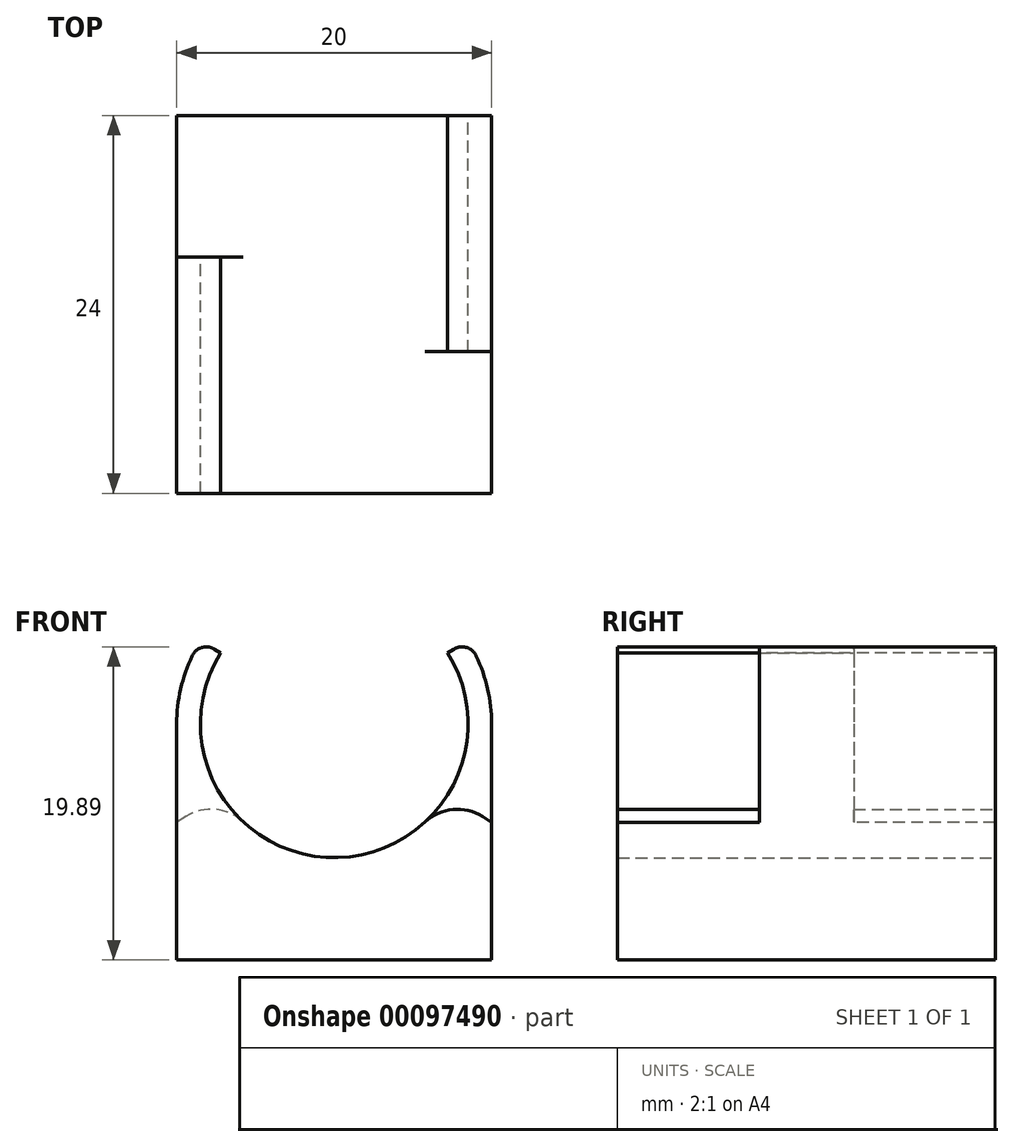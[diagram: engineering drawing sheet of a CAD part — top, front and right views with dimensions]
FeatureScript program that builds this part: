
annotation { "Feature Type Name" : "Feature", "Feature Type Description" : "" }
export const myFeature = defineFeature(function(context is Context, id is Id, definition is map)
    precondition{}
    {
        {
            var Q0;
            Q0=qCreatedBy(makeId("Front.planeOp"),FACE);
            var sketch = newSketch(context, id + "F0", { "sketchPlane" : qUnion([Q0])});
            skCircle(sketch, "E0", {"center": v(0, 0) * mm, "radius": 8.5 * mm});
            skCircle(sketch, "E1", {"center": v(0, 0) * mm, "radius": 10 * mm});
            skLineSegment(sketch, "E2", {"start": v(0, 10) * mm, "end": v(0, -10) * mm, "construction": true});
            skLineSegment(sketch, "E3", {"start": v(-8.48, 5.3) * mm, "end": v(0, 0) * mm});
            skLineSegment(sketch, "E4.MirrorCS", {"start": v(8.48, 5.3) * mm, "end": v(0, 0) * mm});
            skLineSegment(sketch, "E5.top", {"start": v(-10, -10) * mm, "end": v(10, -10) * mm});
            skLineSegment(sketch, "E5.left", {"start": v(-10, 0) * mm, "end": v(-10, -10) * mm});
            skLineSegment(sketch, "E5.right", {"start": v(10, 0) * mm, "end": v(10, -10) * mm});
            skLineSegment(sketch, "E6", {"start": v(0, -10) * mm, "end": v(0, -8.5) * mm});
            skLineSegment(sketch, "E7", {"start": v(0, 0) * mm, "end": v(10, -6.25) * mm});
            skLineSegment(sketch, "E8.MirrorCS", {"start": v(0, 0) * mm, "end": v(-10, -6.25) * mm});
            skSolve(sketch);
        }
        {
            var Q0;
            {var subQ0=sQuery(id+"F0.wireOp",EDGE,"E5.top");var subQ5=sQuery(id+"F0.wireOp",EDGE,"E5.right");var subQ7=makeQuery(id+"F0.imprint","INTERSECT",VERTEX,{"derivedFrom":[subQ0,subQ5]});Q0=makeQuery(id+"F0.imprint","IMPRINT",FACE,{"disambiguationData":[TD([[makeQuery(id+"F0.imprint","IMPRINT",EDGE,{"disambiguationData":[TD([[subQ7,1.0]])],"derivedFrom":subQ5}),-1.0]])]});}
            var Q1;
            {var subQ0=sQuery(id+"F0.wireOp",EDGE,"E5.top");var subQ5=sQuery(id+"F0.wireOp",EDGE,"E5.left");var subQ6=makeQuery(id+"F0.imprint","INTERSECT",VERTEX,{"derivedFrom":[subQ0,subQ5]});Q1=makeQuery(id+"F0.imprint","IMPRINT",FACE,{"disambiguationData":[TD([[makeQuery(id+"F0.imprint","IMPRINT",EDGE,{"disambiguationData":[TD([[subQ6,1.0]])],"derivedFrom":subQ5}),1.0]])]});}
            var Q2;
            {var subQ0=sQuery(id+"F0.wireOp",EDGE,"E6");Q2=makeQuery(id+"F0.imprint","IMPRINT",FACE,{"disambiguationData":[TD([[makeQuery(id+"F0.imprint","IMPRINT",EDGE,{"derivedFrom":subQ0}),-1.0]])]});}
            var Q3;
            {var subQ0=sQuery(id+"F0.wireOp",EDGE,"E6");Q3=makeQuery(id+"F0.imprint","IMPRINT",FACE,{"disambiguationData":[TD([[makeQuery(id+"F0.imprint","IMPRINT",EDGE,{"derivedFrom":subQ0}),1.0]])]});}
            var Q4;
            {var subQ0=sQuery(id+"F0.wireOp",EDGE,"E3");var subQ3=sQuery(id+"F0.wireOp",EDGE,"E0");var subQ4=makeQuery(id+"F0.imprint","INTERSECT",VERTEX,{"derivedFrom":[subQ3,subQ0]});Q4=makeQuery(id+"F0.imprint","IMPRINT",FACE,{"disambiguationData":[TD([[makeQuery(id+"F0.imprint","IMPRINT",EDGE,{"disambiguationData":[TD([[subQ4,-1.0]])],"derivedFrom":subQ3}),-1.0]])]});}
            var Q5;
            {var subQ0=sQuery(id+"F0.wireOp",EDGE,"E5.left");var subQ1=sQuery(id+"F0.wireOp",EDGE,"E1");var subQ2=makeQuery(id+"F0.imprint","INTERSECT",VERTEX,{"derivedFrom":[subQ1,subQ0]});Q5=makeQuery(id+"F0.imprint","IMPRINT",FACE,{"disambiguationData":[TD([[makeQuery(id+"F0.imprint","IMPRINT",EDGE,{"disambiguationData":[TD([[subQ2,-1.0]])],"derivedFrom":subQ1}),-1.0]])]});}
            extrude(context, id + "F1", {"entities" : qUnion([Q0, Q1, Q2, Q3, Q4, Q5]), "flatOperationType" : FlatOperationType.REMOVE, "offsetDistance" : 25 * mm, "depth" : 12 * mm, "hasSecondDirection" : true, "secondDirectionOppositeDirection" : true, "secondDirectionDepth" : 3 * mm, "domain" : OperationDomain.MODEL});
        }
        {
            var Q0;
            {var subQ0=sQuery(id+"F0.wireOp",EDGE,"E5.top");var subQ5=sQuery(id+"F0.wireOp",EDGE,"E5.left");var subQ6=makeQuery(id+"F0.imprint","INTERSECT",VERTEX,{"derivedFrom":[subQ0,subQ5]});Q0=makeQuery(id+"F0.imprint","IMPRINT",FACE,{"disambiguationData":[TD([[makeQuery(id+"F0.imprint","IMPRINT",EDGE,{"disambiguationData":[TD([[subQ6,1.0]])],"derivedFrom":subQ5}),1.0]])]});}
            var Q1;
            {var subQ0=sQuery(id+"F0.wireOp",EDGE,"E6");Q1=makeQuery(id+"F0.imprint","IMPRINT",FACE,{"disambiguationData":[TD([[makeQuery(id+"F0.imprint","IMPRINT",EDGE,{"derivedFrom":subQ0}),-1.0]])]});}
            var Q2;
            {var subQ0=sQuery(id+"F0.wireOp",EDGE,"E6");Q2=makeQuery(id+"F0.imprint","IMPRINT",FACE,{"disambiguationData":[TD([[makeQuery(id+"F0.imprint","IMPRINT",EDGE,{"derivedFrom":subQ0}),1.0]])]});}
            var Q3;
            {var subQ0=sQuery(id+"F0.wireOp",EDGE,"E5.top");var subQ5=sQuery(id+"F0.wireOp",EDGE,"E5.right");var subQ7=makeQuery(id+"F0.imprint","INTERSECT",VERTEX,{"derivedFrom":[subQ0,subQ5]});Q3=makeQuery(id+"F0.imprint","IMPRINT",FACE,{"disambiguationData":[TD([[makeQuery(id+"F0.imprint","IMPRINT",EDGE,{"disambiguationData":[TD([[subQ7,1.0]])],"derivedFrom":subQ5}),-1.0]])]});}
            var Q4;
            {var subQ0=sQuery(id+"F0.wireOp",EDGE,"E4.MirrorCS");var subQ3=sQuery(id+"F0.wireOp",EDGE,"E0");var subQ4=makeQuery(id+"F0.imprint","INTERSECT",VERTEX,{"derivedFrom":[subQ3,subQ0]});Q4=makeQuery(id+"F0.imprint","IMPRINT",FACE,{"disambiguationData":[TD([[makeQuery(id+"F0.imprint","IMPRINT",EDGE,{"disambiguationData":[TD([[subQ4,1.0]])],"derivedFrom":subQ3}),-1.0]])]});}
            var Q5;
            {var subQ0=sQuery(id+"F0.wireOp",EDGE,"E5.right");var subQ1=sQuery(id+"F0.wireOp",EDGE,"E1");var subQ2=makeQuery(id+"F0.imprint","INTERSECT",VERTEX,{"derivedFrom":[subQ1,subQ0]});Q5=makeQuery(id+"F0.imprint","IMPRINT",FACE,{"disambiguationData":[TD([[makeQuery(id+"F0.imprint","IMPRINT",EDGE,{"disambiguationData":[TD([[subQ2,1.0]])],"derivedFrom":subQ1}),-1.0]])]});}
            extrude(context, id + "F2", {"entities" : qUnion([Q0, Q1, Q2, Q3, Q4, Q5]), "operationType" : NewBodyOperationType.ADD, "flatOperationType" : FlatOperationType.REMOVE, "oppositeDirection" : true, "offsetDistance" : 25 * mm, "depth" : 12 * mm, "hasSecondDirection" : true, "secondDirectionOppositeDirection" : false, "secondDirectionDepth" : 3 * mm, "domain" : OperationDomain.MODEL});
        }
        {
            var Q0;
            Q0=makeQuery(id+"F2.opExtrude","SWEPT_EDGE",EDGE,{"disambiguationData":[OSD([sQuery(id+"F0.wireOp",EDGE,"E0"),sQuery(id+"F0.wireOp",EDGE,"E8.MirrorCS")])]});
            var Q1;
            Q1=makeQuery(id+"F1.opExtrude","SWEPT_EDGE",EDGE,{"disambiguationData":[OSD([sQuery(id+"F0.wireOp",EDGE,"E0"),sQuery(id+"F0.wireOp",EDGE,"E7")])]});
            fillet(context, id + "F3", {"entities" : qUnion([Q0, Q1]), "radius" : 3 * mm, "tangentPropagation" : true, "defaultsChanged" : false, "allowEdgeOverflow" : false, "vertexSettings" : [], "filletType" : FilletType.EDGE});
        }
        {
            var Q0;
            Q0=makeQuery(id+"F2.opExtrude","SWEPT_EDGE",EDGE,{"disambiguationData":[OSD([sQuery(id+"F0.wireOp",EDGE,"E1"),sQuery(id+"F0.wireOp",EDGE,"E4.MirrorCS")])]});
            var Q1;
            Q1=makeQuery(id+"F1.opExtrude","SWEPT_EDGE",EDGE,{"disambiguationData":[OSD([sQuery(id+"F0.wireOp",EDGE,"E1"),sQuery(id+"F0.wireOp",EDGE,"E3")])]});
            fillet(context, id + "F4", {"entities" : qUnion([Q0, Q1]), "radius" : 1 * mm, "tangentPropagation" : true, "defaultsChanged" : false, "allowEdgeOverflow" : false, "vertexSettings" : [], "filletType" : FilletType.EDGE});
        }
        {
            var Q0;
            {var subQ0=sQuery(id+"F0.wireOp",EDGE,"E5.top");Q0=makeQuery(id+"F2.boolean.opBoolean","MERGE",FACE,{"derivedFrom":[makeQuery(id+"F1.opExtrude","SWEPT_FACE",FACE,{"disambiguationData":[OSD([subQ0])]}),makeQuery(id+"F2.opExtrude","SWEPT_FACE",FACE,{"disambiguationData":[OSD([subQ0])]})]});}
            extrude(context, id + "F5", {"entities" : qUnion([Q0]), "operationType" : NewBodyOperationType.ADD, "flatOperationType" : FlatOperationType.REMOVE, "offsetDistance" : 25 * mm, "depth" : 5 * mm, "domain" : OperationDomain.MODEL});
        }
    });
